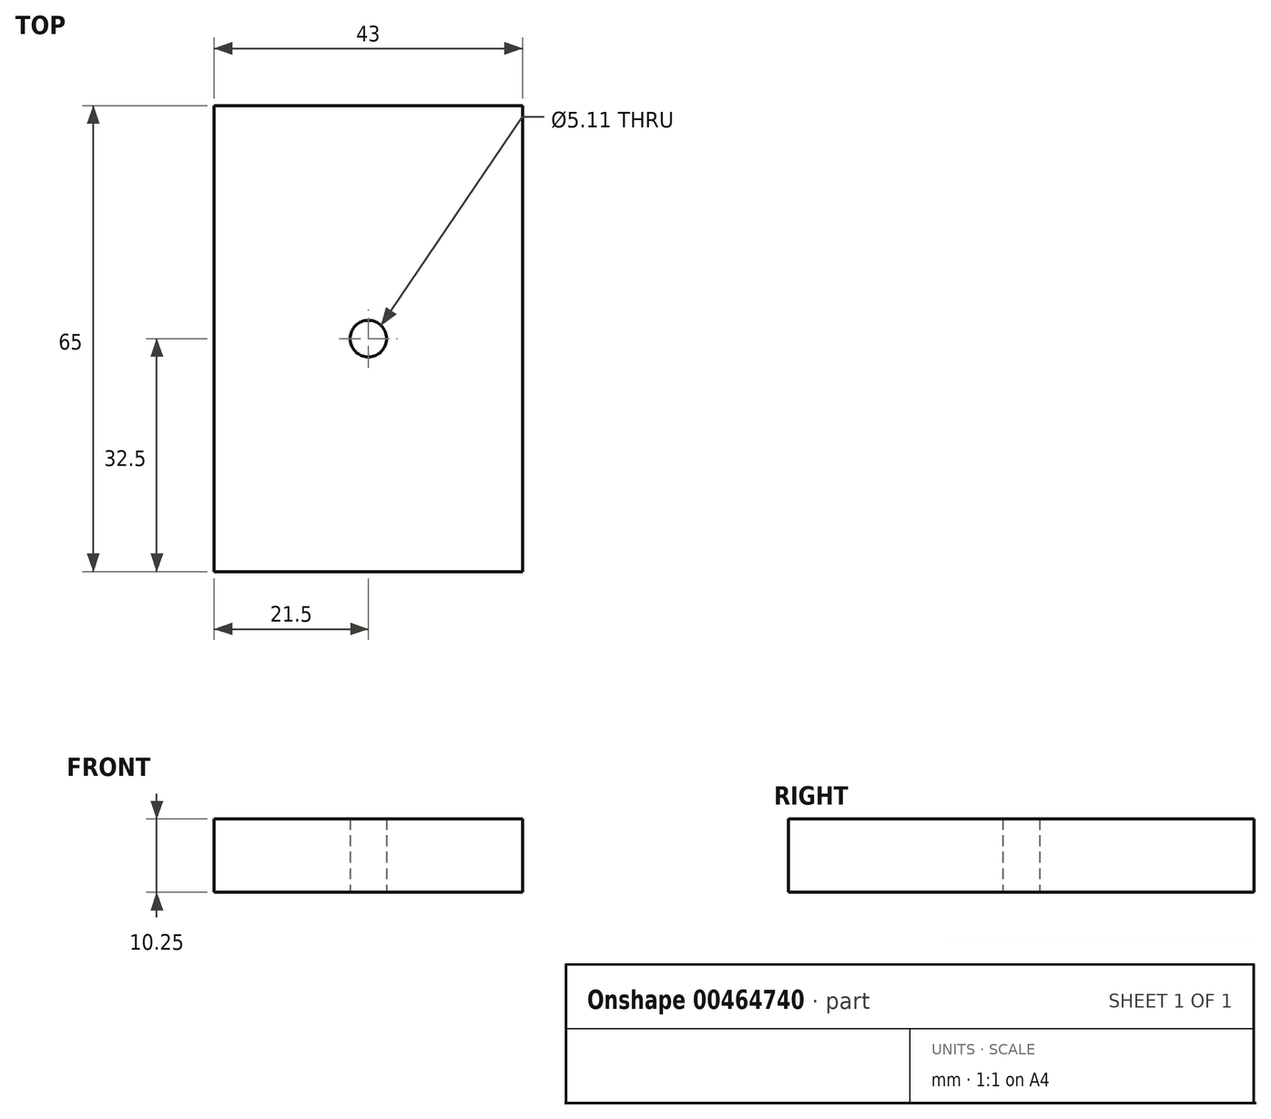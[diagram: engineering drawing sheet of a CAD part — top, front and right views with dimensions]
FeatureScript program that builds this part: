
annotation { "Feature Type Name" : "Feature", "Feature Type Description" : "" }
export const myFeature = defineFeature(function(context is Context, id is Id, definition is map)
    precondition{}
    {
        {
            var Q0;
            Q0=qCreatedBy(makeId("Top.planeOp"),FACE);
            var sketch = newSketch(context, id + "F0", { "sketchPlane" : qUnion([Q0])});
            skLineSegment(sketch, "E0.bottom", {"start": v(21.5, 32.5) * mm, "end": v(-21.5, 32.5) * mm});
            skLineSegment(sketch, "E0.top", {"start": v(21.5, -32.5) * mm, "end": v(-21.5, -32.5) * mm});
            skLineSegment(sketch, "E0.left", {"start": v(21.5, 32.5) * mm, "end": v(21.5, -32.5) * mm});
            skLineSegment(sketch, "E0.right", {"start": v(-21.5, 32.5) * mm, "end": v(-21.5, -32.5) * mm});
            skPoint(sketch, "E0.middle", {"position": v(0, 0) * mm});
            skSolve(sketch);
        }
        {
            var Q0;
            Q0 = qSketchRegion(id + "F0", true);
            extrude(context, id + "F1", {"entities" : qUnion([Q0]), "depth" : 10.25 * mm});
        }
        {
            var Q0;
            Q0=sQuery(id+"F0.wireOp",VERTEX,"E0.middle");
            var Q1;
            Q1=makeQuery(id+"F1.opExtrude","SWEPT_BODY",BODY,{"disambiguationData":[OSD([sQuery(id+"F0.wireOp",EDGE,"E0.bottom"),sQuery(id+"F0.wireOp",EDGE,"E0.top"),sQuery(id+"F0.wireOp",EDGE,"E0.left"),sQuery(id+"F0.wireOp",EDGE,"E0.right")])]});
            hole(context, id + "F2", {"style" : HoleStyle.SIMPLE, "endStyle" : HoleEndStyle.THROUGH, "oppositeDirection" : true, "standardTappedOrClearance" : lookupTablePath({ "standard" : "ANSI", "engagement" : "75%", "pitch" : "20 tpi", "size" : "1/4", "type" : "Tapped" }), "standardBlindInLast" : lookupTablePath({ "standard" : "ANSI", "engagement" : "75%", "pitch" : "20 tpi", "size" : "1/4", "type" : "Tapped" }), "holeDiameter" : 5.1 * mm, "showTappedDepth" : true, "isTappedThrough" : true, "tappedDepth" : 12 * mm, "tapClearance" : 3, "locations" : qUnion([Q0]), "scope" : qUnion([Q1]), "majorDiameter" : 6.35 * mm});
        }
    });
